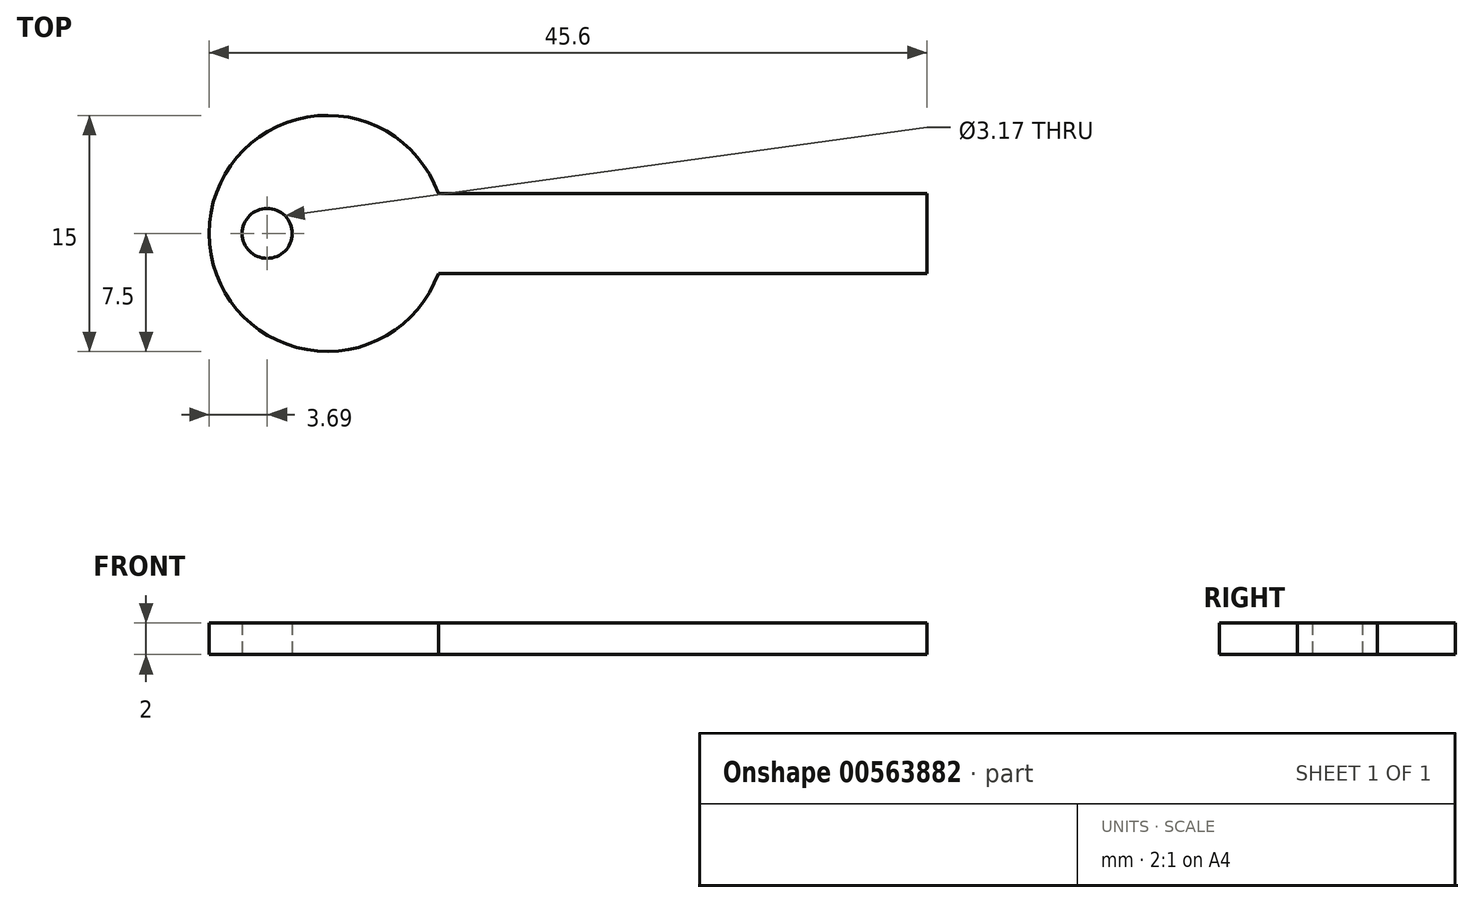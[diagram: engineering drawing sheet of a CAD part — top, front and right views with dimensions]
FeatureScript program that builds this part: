
annotation { "Feature Type Name" : "Feature", "Feature Type Description" : "" }
export const myFeature = defineFeature(function(context is Context, id is Id, definition is map)
    precondition{}
    {
        {
            var Q0;
            Q0=qCreatedBy(makeId("Top.planeOp"),FACE);
            var sketch = newSketch(context, id + "F0", { "sketchPlane" : qUnion([Q0])});
            skCircle(sketch, "E0", {"center": v(0, 0) * mm, "radius": 7.5 * mm});
            skCircle(sketch, "E1", {"center": v(-3.81, 0) * mm, "radius": 1.59 * mm});
            skLineSegment(sketch, "E2.bottom", {"start": v(0, 2.54) * mm, "end": v(38.1, 2.54) * mm});
            skLineSegment(sketch, "E2.top", {"start": v(0, -2.54) * mm, "end": v(38.1, -2.54) * mm});
            skLineSegment(sketch, "E2.left", {"start": v(0, 2.54) * mm, "end": v(0, -2.54) * mm});
            skLineSegment(sketch, "E2.right", {"start": v(38.1, 2.54) * mm, "end": v(38.1, -2.54) * mm});
            skSolve(sketch);
        }
        {
            var Q0;
            Q0 = qSketchRegion(id + "F0", true);
            extrude(context, id + "F1", {"entities" : qUnion([Q0]), "depth" : 2 * mm, "offsetDistance" : 25.4 * mm});
        }
    });
